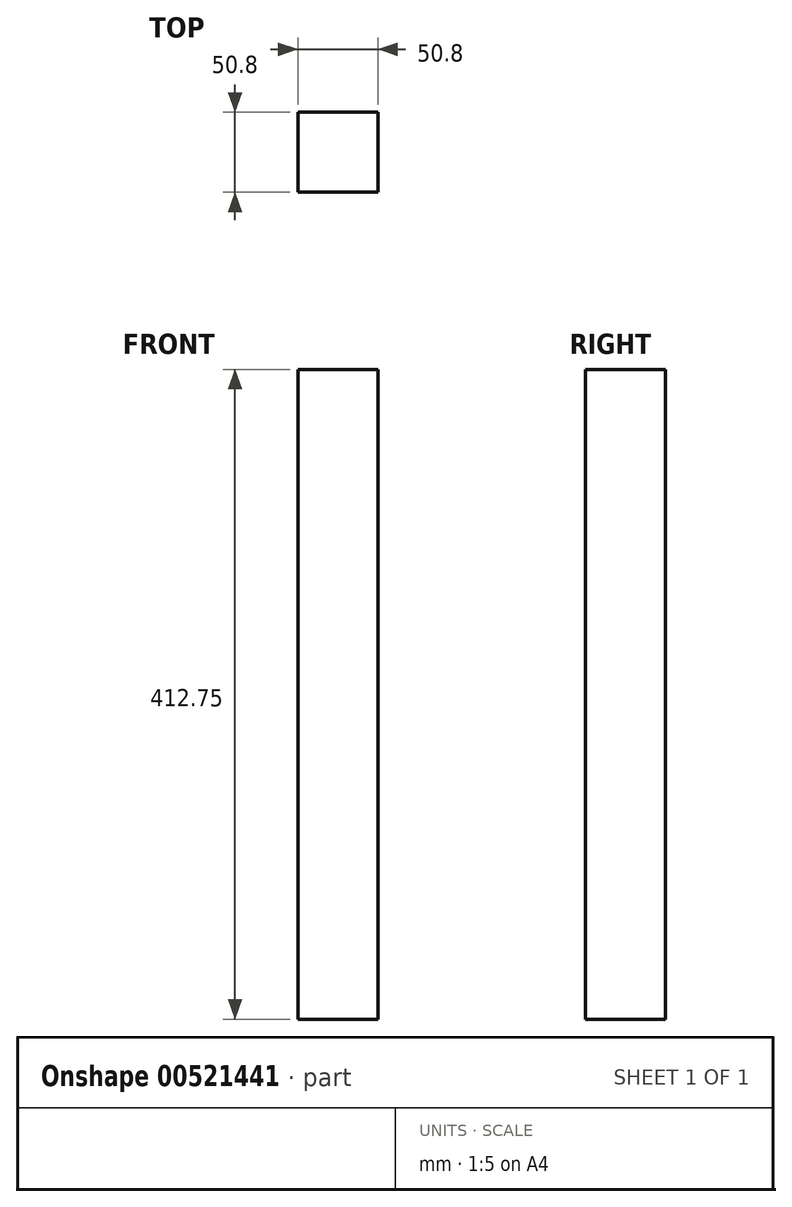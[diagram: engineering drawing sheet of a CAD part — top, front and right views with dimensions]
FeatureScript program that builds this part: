
annotation { "Feature Type Name" : "Feature", "Feature Type Description" : "" }
export const myFeature = defineFeature(function(context is Context, id is Id, definition is map)
    precondition{}
    {
        {
            var Q0;
            Q0=qCreatedBy(makeId("Top.planeOp"),FACE);
            var sketch = newSketch(context, id + "F0", { "sketchPlane" : qUnion([Q0])});
            skLineSegment(sketch, "E0.bottom", {"start": v(-37.03, 17.47) * mm, "end": v(13.77, 17.47) * mm});
            skLineSegment(sketch, "E0.top", {"start": v(-37.03, -33.33) * mm, "end": v(13.77, -33.33) * mm});
            skLineSegment(sketch, "E0.left", {"start": v(-37.03, 17.47) * mm, "end": v(-37.03, -33.33) * mm});
            skLineSegment(sketch, "E0.right", {"start": v(13.77, 17.47) * mm, "end": v(13.77, -33.33) * mm});
            skSolve(sketch);
        }
        {
            var Q0;
            Q0=makeQuery(id+"F0.imprint","IMPRINT",FACE,{"disambiguationData":[TD([[makeQuery(id+"F0.imprint","IMPRINT",EDGE,{"derivedFrom":sQuery(id+"F0.wireOp",EDGE,"E0.bottom")}),-1.0]])]});
            extrude(context, id + "F1", {"entities" : qUnion([Q0]), "depth" : 412.75 * mm, "offsetDistance" : 25.4 * mm});
        }
    });
